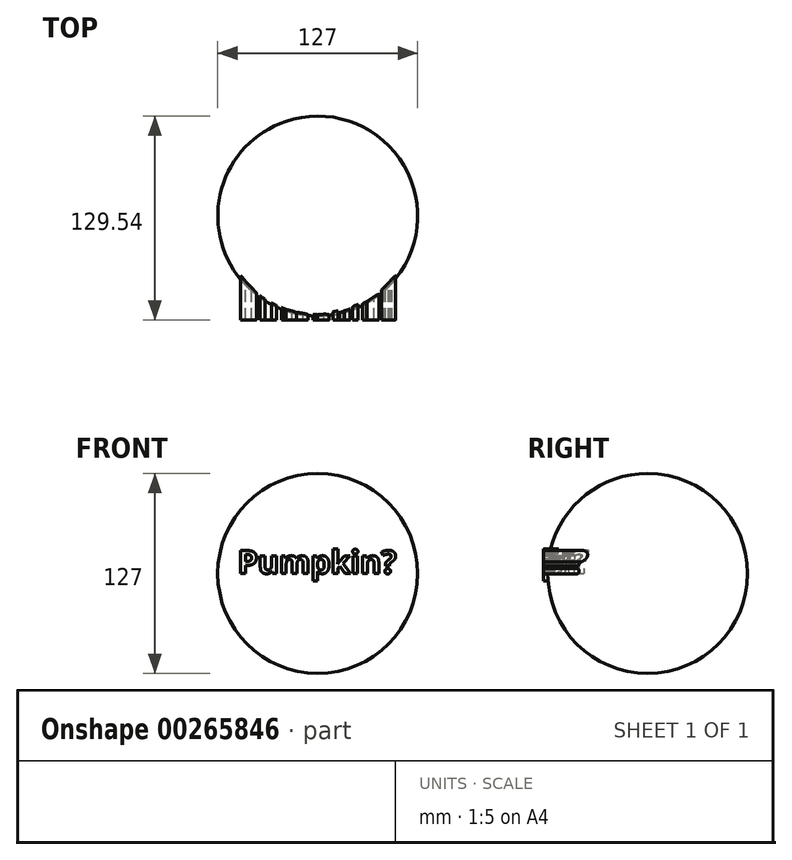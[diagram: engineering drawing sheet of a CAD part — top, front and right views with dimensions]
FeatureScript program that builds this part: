
annotation { "Feature Type Name" : "Feature", "Feature Type Description" : "" }
export const myFeature = defineFeature(function(context is Context, id is Id, definition is map)
    precondition{}
    {
        {
            var Q0;
            Q0=qCreatedBy(makeId("Front.planeOp"),FACE);
            var sketch = newSketch(context, id + "F0", { "sketchPlane" : qUnion([Q0])});
            skArc(sketch, "E0", {"start": v(0, 63.5) * mm, "mid": v(-63.5, 0) * mm, "end": v(0, -63.5) * mm});
            skLineSegment(sketch, "E1", {"start": v(0, 63.5) * mm, "end": v(0, -63.5) * mm});
            skSolve(sketch);
        }
        {
            var Q0;
            Q0 = qSketchRegion(id + "F0", true);
            var Q1;
            Q1=sQuery(id+"F0.wireOp",EDGE,"E1");
            revolve(context, id + "F1", {"entities" : qUnion([Q0]), "axis" : qUnion([Q1]), "revolveType" : RevolveType.FULL});
        }
        {
            var Q0;
            Q0=qCreatedBy(makeId("Front.planeOp"),FACE);
            var sketch = newSketch(context, id + "F2", { "sketchPlane" : qUnion([Q0])});
            skText(sketch, "E2", { "text": "Pumpkin?", "fontName": "OpenSans-Bold.ttf"});
            const initialGuessF2  = {"E2": [-0.0508, 0, 1, 0, 0.01463]};
            skSetInitialGuess(sketch, initialGuessF2);
            skSolve(sketch);
        }
        {
            var Q0;
            Q0 = qSketchRegion(id + "F2", true);
            extrude(context, id + "F3", {"entities" : qUnion([Q0]), "operationType" : NewBodyOperationType.ADD, "depth" : 66.04 * mm});
        }
    });
